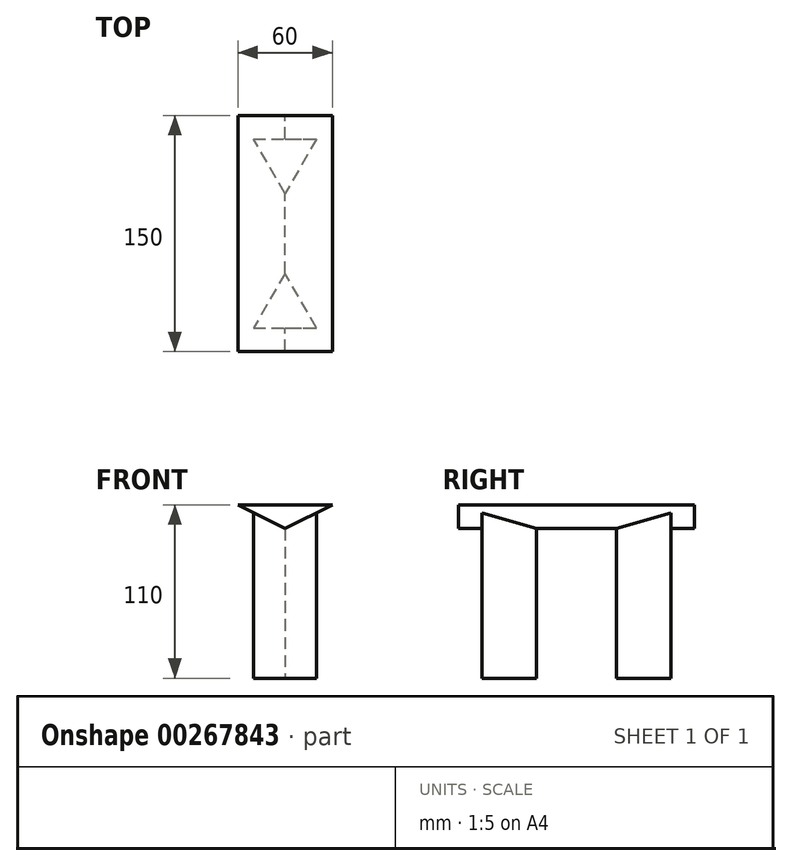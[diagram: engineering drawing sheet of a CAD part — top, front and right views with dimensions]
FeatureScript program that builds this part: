
annotation { "Feature Type Name" : "Feature", "Feature Type Description" : "" }
export const myFeature = defineFeature(function(context is Context, id is Id, definition is map)
    precondition{}
    {
        {
            var Q0;
            Q0=qCreatedBy(makeId("Front.planeOp"),FACE);
            var sketch = newSketch(context, id + "F0", { "sketchPlane" : qUnion([Q0])});
            skLineSegment(sketch, "E0", {"start": v(0, 0) * mm, "end": v(60, 0) * mm});
            skLineSegment(sketch, "E1", {"start": v(60, 0) * mm, "end": v(30, -15) * mm});
            skLineSegment(sketch, "E2", {"start": v(30, -15) * mm, "end": v(0, 0) * mm});
            skSolve(sketch);
        }
        {
            var Q0;
            Q0=makeQuery(id+"F0.imprint","IMPRINT",FACE,{"disambiguationData":[TD([[makeQuery(id+"F0.imprint","IMPRINT",EDGE,{"derivedFrom":sQuery(id+"F0.wireOp",EDGE,"E0")}),-1.0]])]});
            extrude(context, id + "F1", {"entities" : qUnion([Q0]), "depth" : 150 * mm});
        }
        {
            var Q0;
            Q0=makeQuery(id+"F1.opExtrude","SWEPT_FACE",FACE,{"disambiguationData":[OSD([sQuery(id+"F0.wireOp",EDGE,"E0")])]});
            cPlane(context, id + "F2", {"entities" : qUnion([Q0]), "cplaneType" : CPlaneType.OFFSET, "offset" : 110 * mm, "oppositeDirection" : true, "width" : 150 * mm, "height" : 150 * mm});
        }
        {
            var Q0;
            Q0=qCreatedBy(id+"F2.planeOp",FACE);
            var sketch = newSketch(context, id + "F3", { "sketchPlane" : qUnion([Q0])});
            skLineSegment(sketch, "E3.0.0", {"start": v(60, 0) * mm, "end": v(0, 0) * mm});
            skLineSegment(sketch, "E3.0.1", {"start": v(0, 0) * mm, "end": v(0, -150) * mm});
            skLineSegment(sketch, "E3.0.2", {"start": v(0, -150) * mm, "end": v(60, -150) * mm});
            skLineSegment(sketch, "E3.0.3", {"start": v(60, -150) * mm, "end": v(60, 0) * mm});
            skLineSegment(sketch, "E4", {"start": v(10, -135) * mm, "end": v(50, -135) * mm});
            skLineSegment(sketch, "E5", {"start": v(50, -135) * mm, "end": v(30, -100.36) * mm});
            skLineSegment(sketch, "E6", {"start": v(30, -100.36) * mm, "end": v(10, -135) * mm});
            skLineSegment(sketch, "E7", {"start": v(30, 19.08) * mm, "end": v(30, -233.3) * mm, "construction": true});
            skPoint(sketch, "E7.startSnap0", {"position": v(30, 0) * mm});
            skLineSegment(sketch, "E8", {"start": v(0, -75) * mm, "end": v(85.23, -75) * mm, "construction": true});
            skLineSegment(sketch, "E9.MirrorCS", {"start": v(50, -15) * mm, "end": v(30, -49.64) * mm});
            skLineSegment(sketch, "E10.MirrorCS", {"start": v(30, -49.64) * mm, "end": v(10, -15) * mm});
            skLineSegment(sketch, "E11.MirrorCS", {"start": v(10, -15) * mm, "end": v(50, -15) * mm});
            skSolve(sketch);
        }
        {
            var Q0;
            Q0=makeQuery(id+"F3.imprint","IMPRINT",FACE,{"disambiguationData":[TD([[makeQuery(id+"F3.imprint","IMPRINT",EDGE,{"derivedFrom":sQuery(id+"F3.wireOp",EDGE,"E4")}),1.0]])]});
            var Q1;
            Q1=makeQuery(id+"F3.imprint","IMPRINT",FACE,{"disambiguationData":[TD([[makeQuery(id+"F3.imprint","IMPRINT",EDGE,{"derivedFrom":sQuery(id+"F3.wireOp",EDGE,"E9.MirrorCS")}),-1.0]])]});
            extrude(context, id + "F4", {"entities" : qUnion([Q0, Q1]), "operationType" : NewBodyOperationType.ADD, "depth" : 110 * mm});
        }
    });
